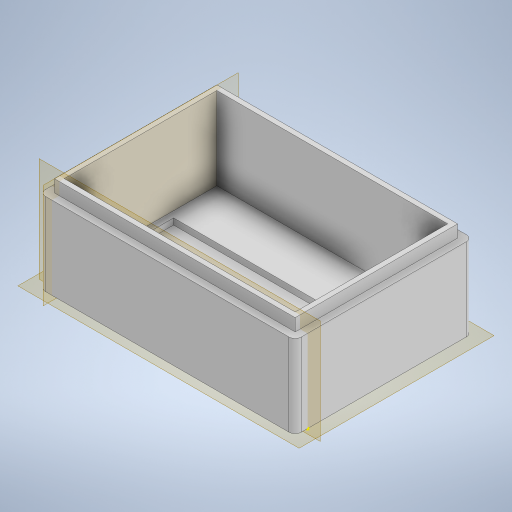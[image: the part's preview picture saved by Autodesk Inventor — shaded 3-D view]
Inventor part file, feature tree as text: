
AUTODESK INVENTOR PART (.ipt)
format: ipt  version: 2024 (Build 280153000, 153)  size: 290,816 bytes
history: native  units: mm
features: sketch x5, extrude x4, fillet x1
ambient origin geometry x8: Origin, YZ Plane, XZ Plane, XY Plane, X Axis, Y Axis, Z Axis, Center Point
bodies: Solid1 (feature_tree)
feature tree (10):
  extrude  "Extrusion1"  Depth=37.0mm
  extrude  "Extrusion2"  Depth=3.0mm
  extrude  "Extrusion3"  Depth=3.0mm
  extrude  "Extrusion4"  TaperAngle=0.0deg  [1 undecoded]
  fillet  "Fillet1"  Radius=53.0mm
  sketch  "Sketch5"  dims[d9=25.0mm d10=0.0mm d12=0.0mm d13=1.5mm d14=0.0mm d15=1.8mm d16=3.0mm d17=0.0mm d18=1.5mm]
  sketch  "Sketch1"  dims[d0=56.0mm d1=37.0mm]
  sketch  "Sketch2"  dims[d2=3.0mm d3=3.0mm]
  sketch  "Sketch3"  dims[d4=0.0mm d5=3.0mm]
  sketch  "Sketch4"  dims[d6=20.0mm d7=0.0mm d8=53.0mm]
note: 1 required parameter value undecoded (feature->parameter linkage not recoverable at this tier; creation-order binding heuristic only, values carry confidence <= 0.55)
